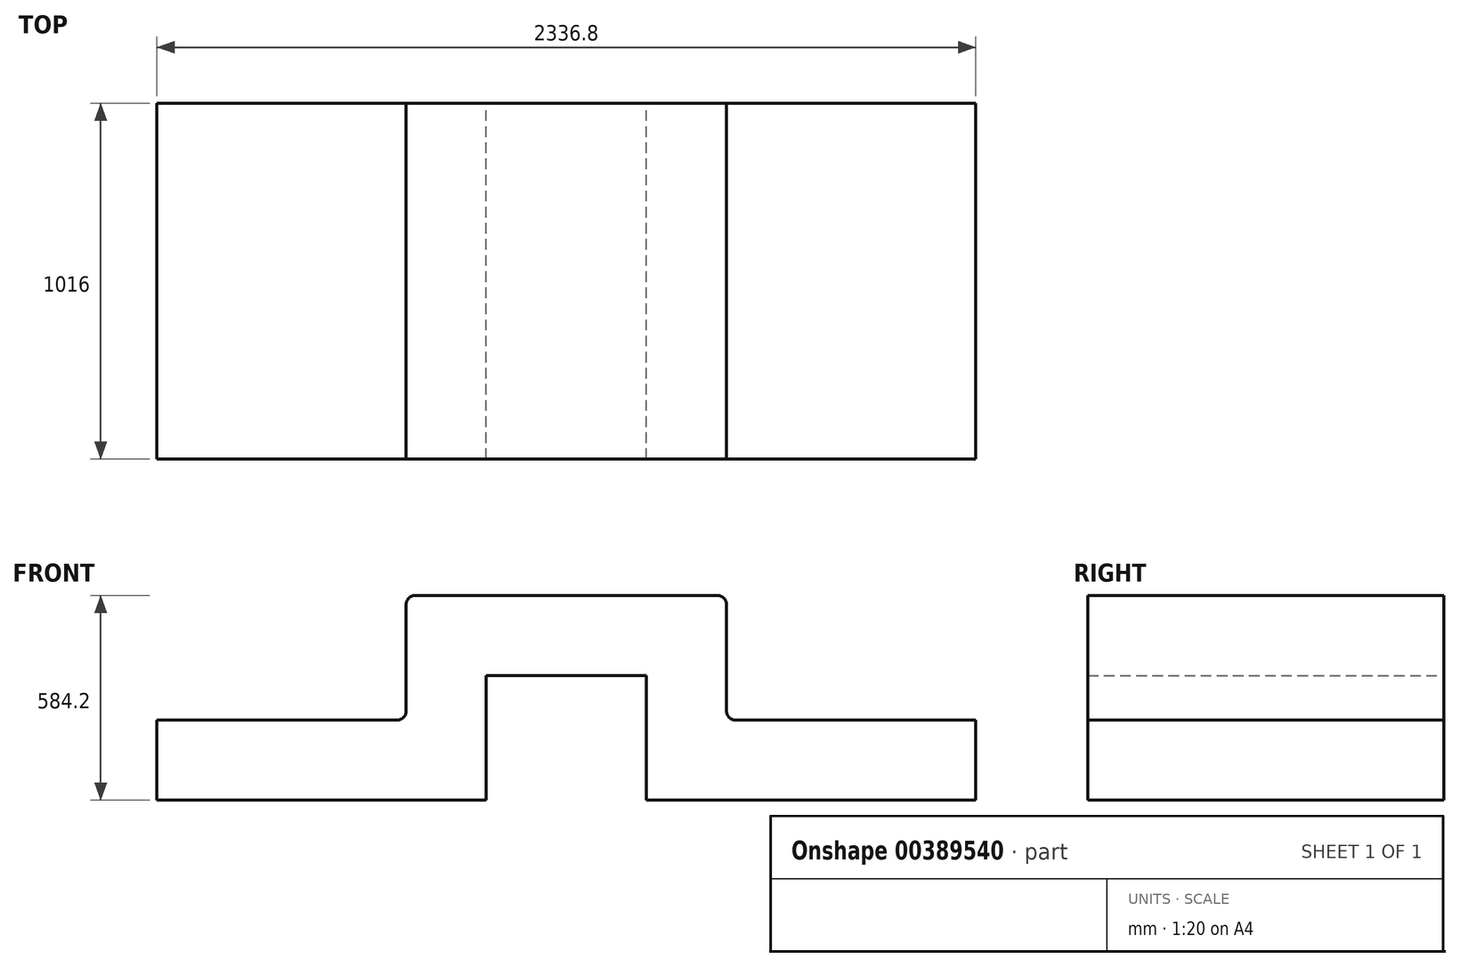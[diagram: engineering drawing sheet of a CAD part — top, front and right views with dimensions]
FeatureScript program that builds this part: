
annotation { "Feature Type Name" : "Feature", "Feature Type Description" : "" }
export const myFeature = defineFeature(function(context is Context, id is Id, definition is map)
    precondition{}
    {
        {
            var Q0;
            Q0=qCreatedBy(makeId("Front.planeOp"),FACE);
            var sketch = newSketch(context, id + "F0", { "sketchPlane" : qUnion([Q0])});
            skLineSegment(sketch, "E0", {"start": v(-1393.38, -254) * mm, "end": v(-453.58, -254) * mm});
            skLineSegment(sketch, "E1", {"start": v(-453.58, -254) * mm, "end": v(-453.58, 101.6) * mm});
            skLineSegment(sketch, "E2", {"start": v(-453.58, 101.6) * mm, "end": v(3.62, 101.6) * mm});
            skLineSegment(sketch, "E3", {"start": v(3.62, 101.6) * mm, "end": v(3.62, -254) * mm});
            skLineSegment(sketch, "E4", {"start": v(3.62, -254) * mm, "end": v(943.42, -254) * mm});
            skLineSegment(sketch, "E5", {"start": v(943.42, -254) * mm, "end": v(943.42, -25.4) * mm});
            skLineSegment(sketch, "E6", {"start": v(943.42, -25.4) * mm, "end": v(257.62, -25.4) * mm});
            skLineSegment(sketch, "E7", {"start": v(232.22, 0) * mm, "end": v(232.22, 304.8) * mm});
            skLineSegment(sketch, "E8", {"start": v(206.82, 330.2) * mm, "end": v(-656.78, 330.2) * mm});
            skLineSegment(sketch, "E9", {"start": v(-682.18, 304.8) * mm, "end": v(-682.18, 0) * mm});
            skLineSegment(sketch, "E10", {"start": v(-707.58, -25.4) * mm, "end": v(-1393.38, -25.4) * mm});
            skLineSegment(sketch, "E11", {"start": v(-1393.38, -25.4) * mm, "end": v(-1393.38, -254) * mm});
            skArc(sketch, "E12", {"start": v(-656.78, 330.2) * mm, "mid": v(-674.74, 322.76) * mm, "end": v(-682.18, 304.8) * mm});
            skArc(sketch, "E13", {"start": v(232.22, 304.8) * mm, "mid": v(224.79, 322.76) * mm, "end": v(206.82, 330.2) * mm});
            skArc(sketch, "E14", {"start": v(232.22, 0) * mm, "mid": v(239.66, -17.96) * mm, "end": v(257.62, -25.4) * mm});
            skArc(sketch, "E15", {"start": v(-707.58, -25.4) * mm, "mid": v(-689.61, -17.96) * mm, "end": v(-682.18, 0) * mm});
            skSolve(sketch);
        }
        {
            var Q0;
            Q0=makeQuery(id+"F0.imprint","IMPRINT",FACE,{"disambiguationData":[TD([[makeQuery(id+"F0.imprint","IMPRINT",EDGE,{"derivedFrom":sQuery(id+"F0.wireOp",EDGE,"E0")}),1.0]])]});
            extrude(context, id + "F1", {"entities" : qUnion([Q0]), "depth" : 1016 * mm});
        }
    });
